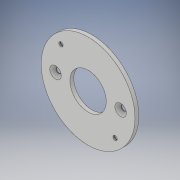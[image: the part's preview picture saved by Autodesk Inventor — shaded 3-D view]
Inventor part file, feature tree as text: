
AUTODESK INVENTOR PART (.ipt)
format: ipt  version: 2019 (Build 230136000, 136)  size: 133,632 bytes
history: native  units: mm
features: sketch x4, extrude x2, hole x2
ambient origin geometry x8: Origin, YZ Plane, XZ Plane, XY Plane, X Axis, Y Axis, Z Axis, Center Point
bodies: Solid1 (feature_tree)
feature tree (8):
  extrude  "Extrusion1"  Depth=4.0mm TaperAngle=0.0deg
  hole  "Hole1"  [1 undecoded]
  hole  "Hole2"  [1 undecoded]
  extrude  "Extrusion2"  Depth=10.0mm
  sketch  "Sketch1"  dims[d0=98.0mm d1=4.0mm d2=0.0mm]
  sketch  "Sketch2"  dims[d3=68.0mm d4=55.0mm]
  sketch  "Sketch3"  dims[d5=5.5mm d6=6.0mm d7=12.0mm d8=2.0mm d9=90.0deg d10=26.75mm d11=0.0mm d12=70.0mm]
  sketch  "Sketch4"  dims[d13=70.0mm d14=120.0mm d15=80.0mm d16=4.5mm d17=6.0mm d18=10.0mm d19=2.0mm d20=90.0deg d21=26.75mm d22=0.0mm d23=38.0mm d24=10.0mm d25=0.0mm]
note: 2 required parameter values undecoded (feature->parameter linkage not recoverable at this tier; creation-order binding heuristic only, values carry confidence <= 0.55)
